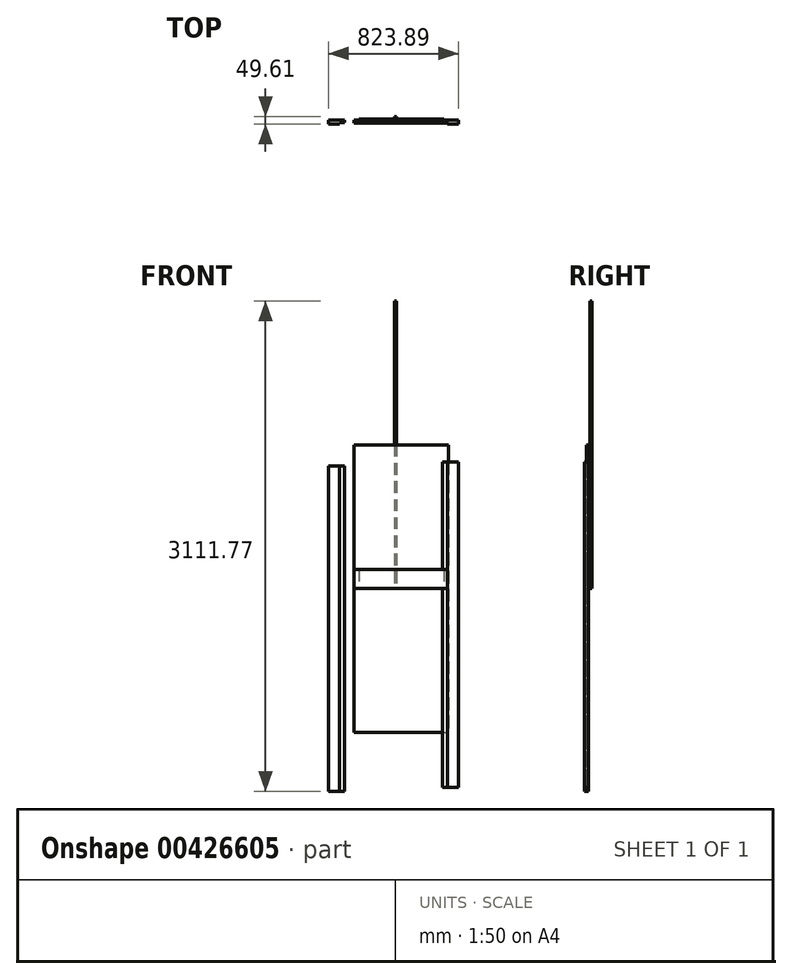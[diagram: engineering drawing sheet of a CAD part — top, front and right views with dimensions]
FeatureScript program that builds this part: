
annotation { "Feature Type Name" : "Feature", "Feature Type Description" : "" }
export const myFeature = defineFeature(function(context is Context, id is Id, definition is map)
    precondition{}
    {
        {
            var Q0;
            Q0=qCreatedBy(makeId("Top.planeOp"),FACE);
            var sketch = newSketch(context, id + "F0", { "sketchPlane" : qUnion([Q0])});
            skLineSegment(sketch, "E0.bottom", {"start": v(-270, 7.5) * mm, "end": v(270, 7.5) * mm});
            skLineSegment(sketch, "E0.left", {"start": v(-270, 7.5) * mm, "end": v(-270, -7.5) * mm});
            skLineSegment(sketch, "E0.right", {"start": v(270, 7.5) * mm, "end": v(270, -7.5) * mm});
            skPoint(sketch, "E0.middle", {"position": v(0, 0) * mm});
            skLineSegment(sketch, "E1.bottom", {"start": v(-300, -7.5) * mm, "end": v(-270, -7.5) * mm});
            skLineSegment(sketch, "E1.top", {"start": v(-300, -17.5) * mm, "end": v(300, -17.5) * mm});
            skLineSegment(sketch, "E1.left", {"start": v(-300, -7.5) * mm, "end": v(-300, -17.5) * mm});
            skLineSegment(sketch, "E1.right", {"start": v(300, -7.5) * mm, "end": v(300, -17.5) * mm});
            skPoint(sketch, "E1.middle", {"position": v(0, -12.5) * mm});
            skLineSegment(sketch, "E2.trimOffspring", {"start": v(270, -7.5) * mm, "end": v(300, -7.5) * mm});
            skSolve(sketch);
        }
        {
            var Q0;
            Q0 = qSketchRegion(id + "F0", true);
            extrude(context, id + "F1", {"entities" : qUnion([Q0]), "depth" : 120 * mm});
        }
        {
            var Q0;
            Q0=qCreatedBy(makeId("Front.planeOp"),FACE);
            var sketch = newSketch(context, id + "F2", { "sketchPlane" : qUnion([Q0])});
            skLineSegment(sketch, "E3.bottom", {"start": v(-461.75, 778.23) * mm, "end": v(-391.75, 778.23) * mm});
            skLineSegment(sketch, "E3.top", {"start": v(-461.75, -1286.77) * mm, "end": v(-361.75, -1286.77) * mm});
            skLineSegment(sketch, "E3.left", {"start": v(-461.75, 778.23) * mm, "end": v(-461.75, -1286.77) * mm});
            skLineSegment(sketch, "E3.right", {"start": v(-361.75, 778.23) * mm, "end": v(-361.75, -1286.77) * mm});
            skPoint(sketch, "E3.middle", {"position": v(-411.75, -254.27) * mm});
            skLineSegment(sketch, "E4", {"start": v(-391.75, 778.23) * mm, "end": v(-391.75, -1286.77) * mm});
            skLineSegment(sketch, "E5", {"start": v(-391.75, 778.23) * mm, "end": v(-361.75, 778.23) * mm});
            skSolve(sketch);
        }
        {
            var Q0;
            Q0=makeQuery(id+"F2.imprint","IMPRINT",FACE,{"disambiguationData":[TD([[makeQuery(id+"F2.imprint","IMPRINT",EDGE,{"derivedFrom":sQuery(id+"F2.wireOp",EDGE,"E3.bottom")}),-1.0]])]});
            extrude(context, id + "F3", {"entities" : qUnion([Q0]), "depth" : 25 * mm});
        }
        {
            var Q0;
            {var subQ0=sQuery(id+"F2.wireOp",EDGE,"E3.right");Q0=makeQuery(id+"F2.imprint","IMPRINT",FACE,{"disambiguationData":[TD([[makeQuery(id+"F2.imprint","IMPRINT",EDGE,{"derivedFrom":subQ0}),-1.0]])]});}
            extrude(context, id + "F4", {"entities" : qUnion([Q0]), "operationType" : NewBodyOperationType.ADD, "depth" : 15 * mm});
        }
        {
            var Q0;
            Q0=qCreatedBy(makeId("Front.planeOp"),FACE);
            var sketch = newSketch(context, id + "F5", { "sketchPlane" : qUnion([Q0])});
            skLineSegment(sketch, "E6.MirrorCS", {"start": v(292.14, 803.07) * mm, "end": v(262.14, 803.07) * mm});
            skLineSegment(sketch, "E7.MirrorCS", {"start": v(362.14, 803.07) * mm, "end": v(292.14, 803.07) * mm});
            skLineSegment(sketch, "E8.MirrorCS", {"start": v(362.14, -1261.93) * mm, "end": v(262.14, -1261.93) * mm});
            skLineSegment(sketch, "E9.MirrorCS", {"start": v(362.14, 803.07) * mm, "end": v(362.14, -1261.93) * mm});
            skLineSegment(sketch, "E10.MirrorCS", {"start": v(262.14, 803.07) * mm, "end": v(262.14, -1261.93) * mm});
            skLineSegment(sketch, "E11.MirrorCS", {"start": v(292.14, 803.07) * mm, "end": v(292.14, -1261.93) * mm});
            skPoint(sketch, "E12.MirrorP", {"position": v(312.14, -229.43) * mm});
            skSolve(sketch);
        }
        {
            var Q0;
            Q0=makeQuery(id+"F5.imprint","IMPRINT",FACE,{"disambiguationData":[TD([[makeQuery(id+"F5.imprint","IMPRINT",EDGE,{"derivedFrom":sQuery(id+"F5.wireOp",EDGE,"E7.MirrorCS")}),1.0]])]});
            extrude(context, id + "F6", {"entities" : qUnion([Q0]), "depth" : 25 * mm});
        }
        {
            var Q0;
            Q0=makeQuery(id+"F5.imprint","IMPRINT",FACE,{"disambiguationData":[TD([[makeQuery(id+"F5.imprint","IMPRINT",EDGE,{"derivedFrom":sQuery(id+"F5.wireOp",EDGE,"E6.MirrorCS")}),1.0]])]});
            extrude(context, id + "F7", {"entities" : qUnion([Q0]), "operationType" : NewBodyOperationType.ADD, "depth" : 15 * mm});
        }
        {
            var Q0;
            Q0=qCreatedBy(makeId("Front.planeOp"),FACE);
            var sketch = newSketch(context, id + "F8", { "sketchPlane" : qUnion([Q0])});
            skLineSegment(sketch, "E13.bottom", {"start": v(-300, 912.5) * mm, "end": v(300, 912.5) * mm});
            skLineSegment(sketch, "E13.top", {"start": v(-300, -912.5) * mm, "end": v(300, -912.5) * mm});
            skLineSegment(sketch, "E13.left", {"start": v(-300, 912.5) * mm, "end": v(-300, -912.5) * mm});
            skLineSegment(sketch, "E13.right", {"start": v(300, 912.5) * mm, "end": v(300, -912.5) * mm});
            skPoint(sketch, "E13.middle", {"position": v(0, 0) * mm});
            skSolve(sketch);
        }
        {
            var Q0;
            Q0=makeQuery(id+"F8.imprint","IMPRINT",FACE,{"disambiguationData":[TD([[makeQuery(id+"F8.imprint","IMPRINT",EDGE,{"derivedFrom":sQuery(id+"F8.wireOp",EDGE,"E13.bottom")}),-1.0]])]});
            extrude(context, id + "F9", {"entities" : qUnion([Q0]), "depth" : 10 * mm});
        }
        {
            var Q0;
            Q0=qCreatedBy(makeId("Top.planeOp"),FACE);
            var sketch = newSketch(context, id + "F10", { "sketchPlane" : qUnion([Q0])});
            skLineSegment(sketch, "E14.bottom", {"start": v(-44.54, 24.61) * mm, "end": v(-29.54, 24.61) * mm});
            skLineSegment(sketch, "E14.top", {"start": v(-44.54, 9.61) * mm, "end": v(-29.54, 9.61) * mm});
            skLineSegment(sketch, "E14.left", {"start": v(-44.54, 24.61) * mm, "end": v(-44.54, 9.61) * mm});
            skLineSegment(sketch, "E14.right", {"start": v(-29.54, 24.61) * mm, "end": v(-29.54, 9.61) * mm});
            skPoint(sketch, "E14.middle", {"position": v(-37.04, 17.11) * mm});
            skSolve(sketch);
        }
        {
            var Q0;
            Q0 = qSketchRegion(id + "F10", true);
            extrude(context, id + "F11", {"entities" : qUnion([Q0]), "depth" : 1825 * mm});
        }
    });
